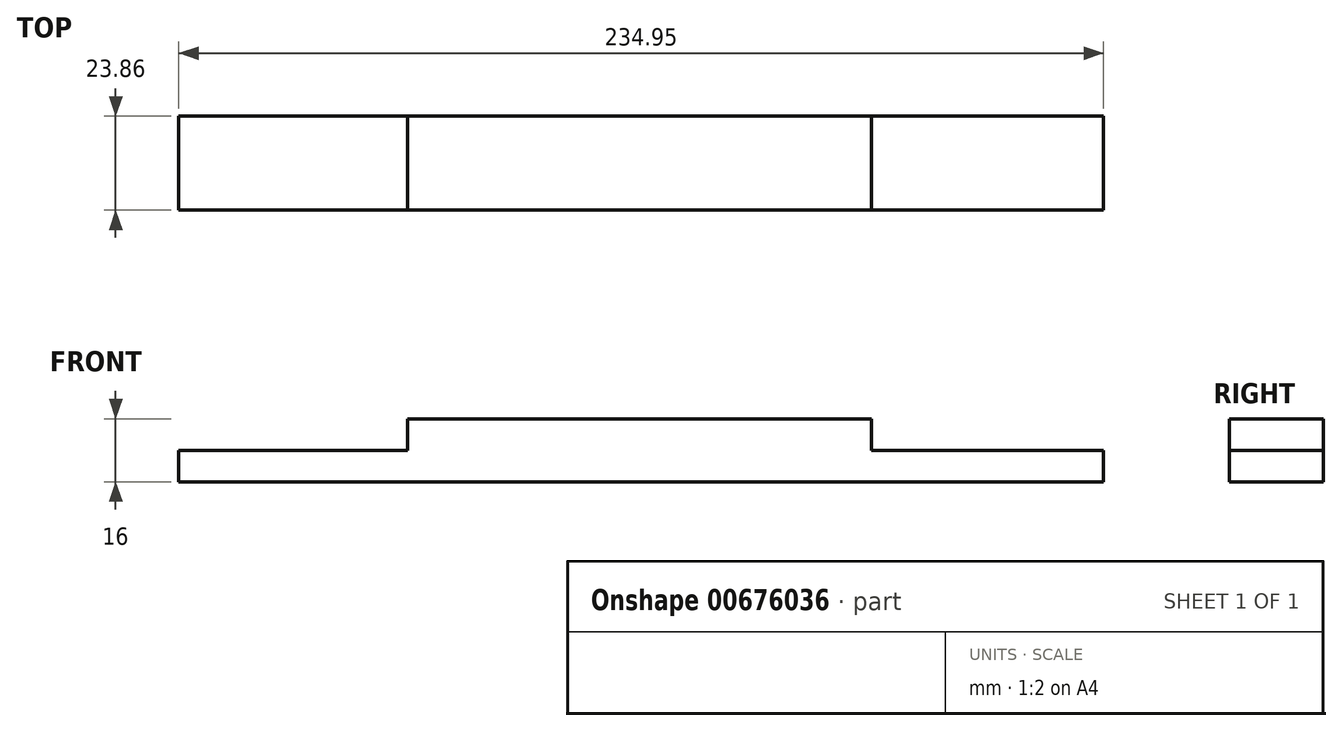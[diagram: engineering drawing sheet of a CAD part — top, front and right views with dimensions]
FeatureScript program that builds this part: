
annotation { "Feature Type Name" : "Feature", "Feature Type Description" : "" }
export const myFeature = defineFeature(function(context is Context, id is Id, definition is map)
    precondition{}
    {
        {
            var Q0;
            Q0=qCreatedBy(makeId("Front.planeOp"),FACE);
            var sketch = newSketch(context, id + "F0", { "sketchPlane" : qUnion([Q0])});
            skLineSegment(sketch, "E0", {"start": v(-147.28, -36.58) * mm, "end": v(87.67, -36.58) * mm});
            skLineSegment(sketch, "E1", {"start": v(87.67, -36.58) * mm, "end": v(87.67, -28.58) * mm});
            skLineSegment(sketch, "E2", {"start": v(87.67, -28.58) * mm, "end": v(28.74, -28.58) * mm});
            skLineSegment(sketch, "E3", {"start": v(28.74, -28.58) * mm, "end": v(28.74, -20.58) * mm});
            skLineSegment(sketch, "E4", {"start": v(28.74, -20.58) * mm, "end": v(-89.11, -20.58) * mm});
            skLineSegment(sketch, "E5", {"start": v(-89.11, -20.58) * mm, "end": v(-89.11, -28.58) * mm});
            skLineSegment(sketch, "E6", {"start": v(-89.11, -28.58) * mm, "end": v(-147.28, -28.58) * mm});
            skLineSegment(sketch, "E7", {"start": v(-147.28, -28.58) * mm, "end": v(-147.28, -36.58) * mm});
            skSolve(sketch);
        }
        {
            var Q0;
            Q0=makeQuery(id+"F0.imprint","IMPRINT",FACE,{"disambiguationData":[TD([[makeQuery(id+"F0.imprint","IMPRINT",EDGE,{"derivedFrom":sQuery(id+"F0.wireOp",EDGE,"E0")}),1.0]])]});
            extrude(context, id + "F1", {"entities" : qUnion([Q0]), "depth" : 23.86 * mm, "offsetDistance" : 25.4 * mm});
        }
    });
